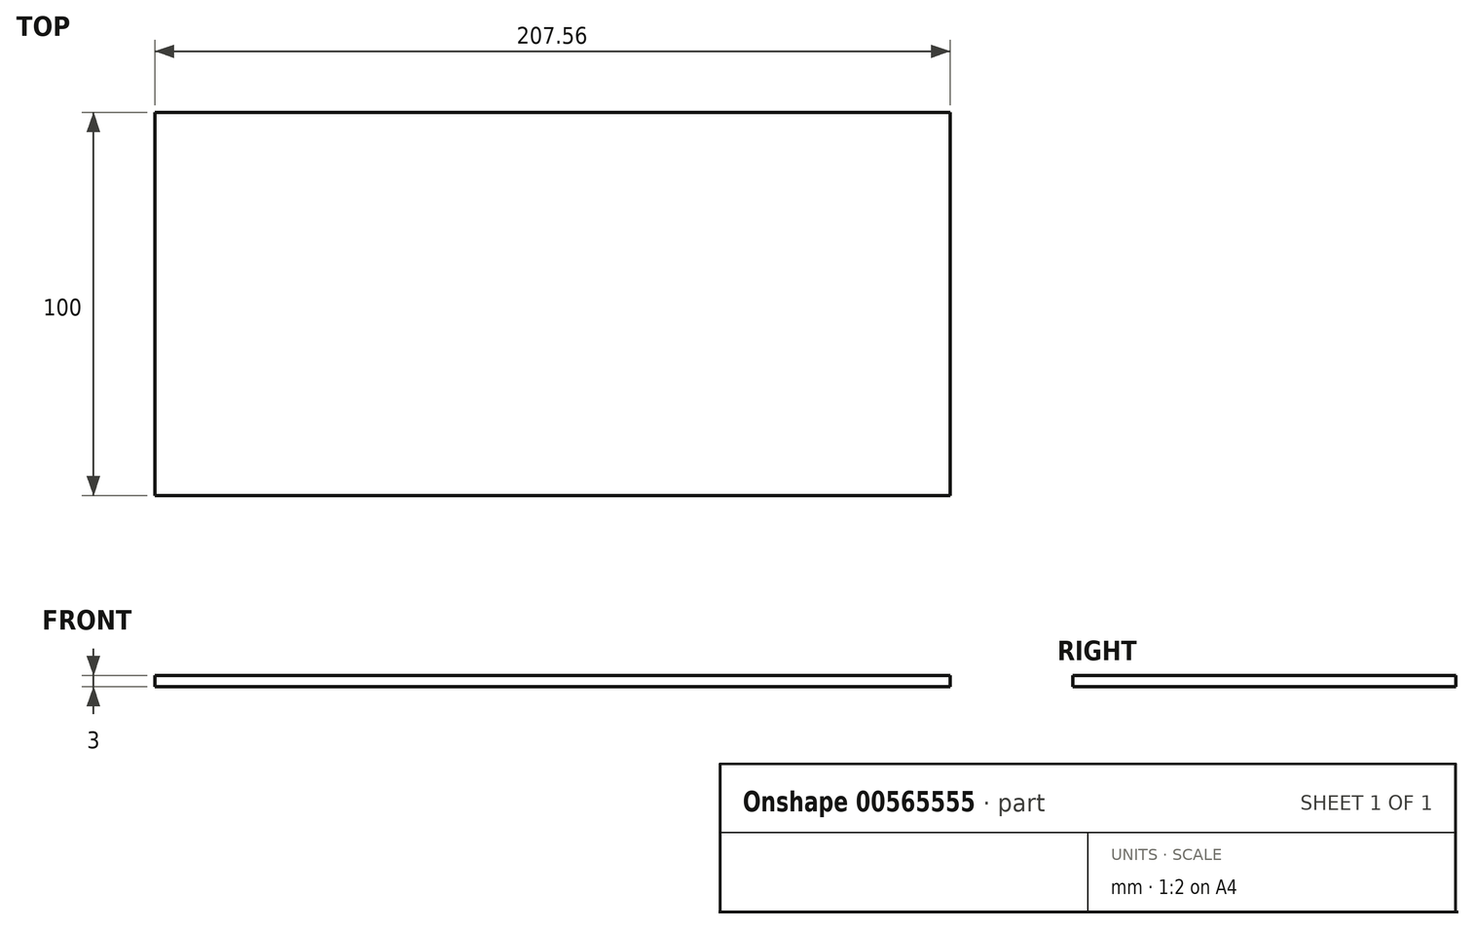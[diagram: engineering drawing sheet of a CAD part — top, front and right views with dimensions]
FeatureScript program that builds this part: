
annotation { "Feature Type Name" : "Feature", "Feature Type Description" : "" }
export const myFeature = defineFeature(function(context is Context, id is Id, definition is map)
    precondition{}
    {
        {
            var Q0;
            Q0=qCreatedBy(makeId("Top.planeOp"),FACE);
            var sketch = newSketch(context, id + "F0", { "sketchPlane" : qUnion([Q0])});
            skLineSegment(sketch, "E0.bottom", {"start": v(103.78, -50) * mm, "end": v(-103.78, -50) * mm});
            skLineSegment(sketch, "E0.top", {"start": v(103.78, 50) * mm, "end": v(-103.78, 50) * mm});
            skLineSegment(sketch, "E0.left", {"start": v(103.78, -50) * mm, "end": v(103.78, 50) * mm});
            skLineSegment(sketch, "E0.right", {"start": v(-103.78, -50) * mm, "end": v(-103.78, 50) * mm});
            skPoint(sketch, "E0.middle", {"position": v(0, 0) * mm});
            skSolve(sketch);
        }
        {
            var Q0;
            Q0 = qSketchRegion(id + "F0", true);
            extrude(context, id + "F1", {"entities" : qUnion([Q0]), "depth" : 3 * mm, "offsetDistance" : 25 * mm});
        }
    });
